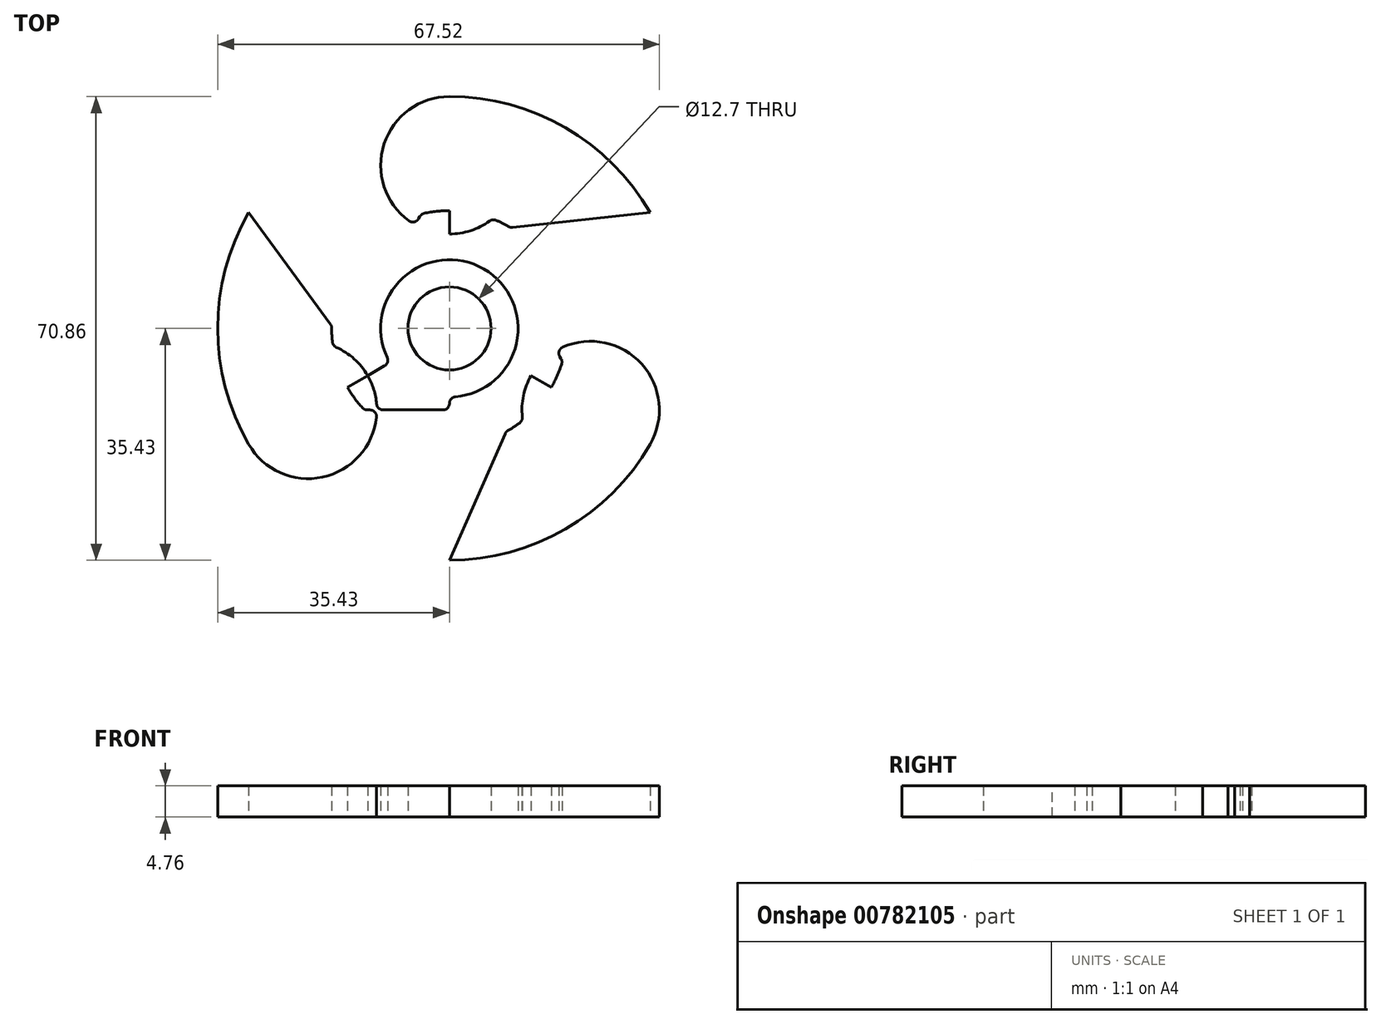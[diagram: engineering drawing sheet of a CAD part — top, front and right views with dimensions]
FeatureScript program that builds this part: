
annotation { "Feature Type Name" : "Feature", "Feature Type Description" : "" }
export const myFeature = defineFeature(function(context is Context, id is Id, definition is map)
    precondition{}
    {
        {
            var Q0;
            Q0=qCreatedBy(makeId("Top.planeOp"),FACE);
            var sketch = newSketch(context, id + "F0", { "sketchPlane" : qUnion([Q0])});
            skCircle(sketch, "E0", {"center": v(0, 0) * mm, "radius": 6.35 * mm});
            skCircle(sketch, "E1", {"center": v(0, 0) * mm, "radius": 10.5 * mm});
            skCircle(sketch, "E2", {"center": v(0, 0) * mm, "radius": 18 * mm});
            skCircle(sketch, "E3", {"center": v(0, 0) * mm, "radius": 24.93 * mm});
            skLineSegment(sketch, "E4", {"start": v(0, 0) * mm, "end": v(21.6, -12.46) * mm});
            skLineSegment(sketch, "E5", {"start": v(0, 0) * mm, "end": v(-21.59, -12.46) * mm});
            skLineSegment(sketch, "E6", {"start": v(0, 0) * mm, "end": v(0, 24.93) * mm});
            skLineSegment(sketch, "E7", {"start": v(0, 24.93) * mm, "end": v(-21.6, -12.46) * mm});
            skLineSegment(sketch, "E8", {"start": v(-21.59, -12.46) * mm, "end": v(21.59, -12.46) * mm});
            skLineSegment(sketch, "E9", {"start": v(0, 24.93) * mm, "end": v(21.6, -12.46) * mm});
            skCircle(sketch, "E10", {"center": v(0, 24.93) * mm, "radius": 10.5 * mm});
            skCircle(sketch, "E11", {"center": v(21.6, -12.46) * mm, "radius": 10.5 * mm});
            skCircle(sketch, "E12", {"center": v(-21.59, -12.46) * mm, "radius": 10.5 * mm});
            skCircle(sketch, "E13", {"center": v(0, 0) * mm, "radius": 35.43 * mm});
            skLineSegment(sketch, "E14", {"start": v(0, 0) * mm, "end": v(-21.6, 12.46) * mm});
            skLineSegment(sketch, "E15", {"start": v(0, 0) * mm, "end": v(21.59, 12.46) * mm});
            skLineSegment(sketch, "E16", {"start": v(0, 0) * mm, "end": v(0, -24.93) * mm});
            skPoint(sketch, "E16.endSnap0", {"position": v(0, -12.46) * mm});
            skLineSegment(sketch, "E17", {"start": v(0, 0) * mm, "end": v(-30.68, -17.71) * mm});
            skLineSegment(sketch, "E18", {"start": v(0, 0) * mm, "end": v(30.68, -17.71) * mm});
            skLineSegment(sketch, "E19", {"start": v(0, 0) * mm, "end": v(0, 35.43) * mm});
            skLineSegment(sketch, "E20", {"start": v(0, 0) * mm, "end": v(-30.68, 17.71) * mm});
            skLineSegment(sketch, "E21", {"start": v(0, 0) * mm, "end": v(0, -35.43) * mm});
            skLineSegment(sketch, "E22", {"start": v(0, 0) * mm, "end": v(30.68, 17.71) * mm});
            skLineSegment(sketch, "E23", {"start": v(-30.68, 17.71) * mm, "end": v(-13.14, -6.23) * mm});
            skPoint(sketch, "E23.endSnap0", {"position": v(-10.8, -6.23) * mm});
            skLineSegment(sketch, "E24", {"start": v(30.68, 17.71) * mm, "end": v(0, 14.37) * mm});
            skLineSegment(sketch, "E25", {"start": v(0, -35.43) * mm, "end": v(12.44, -7.18) * mm});
            skSolve(sketch);
        }
        {
            var Q0;
            {var subQ0=sQuery(id+"F0.wireOp",EDGE,"E20");var subQ1=sQuery(id+"F0.wireOp",EDGE,"E0");var subQ2=makeQuery(id+"F0.imprint","INTERSECT",VERTEX,{"derivedFrom":[subQ1,subQ0]});Q0=makeQuery(id+"F0.imprint","IMPRINT",FACE,{"disambiguationData":[TD([[makeQuery(id+"F0.imprint","IMPRINT",EDGE,{"disambiguationData":[TD([[subQ2,-1.0]])],"derivedFrom":subQ1}),-1.0]])]});}
            var Q1;
            {var subQ0=sQuery(id+"F0.wireOp",EDGE,"E17");var subQ1=sQuery(id+"F0.wireOp",EDGE,"E0");var subQ2=makeQuery(id+"F0.imprint","INTERSECT",VERTEX,{"derivedFrom":[subQ1,subQ0]});Q1=makeQuery(id+"F0.imprint","IMPRINT",FACE,{"disambiguationData":[TD([[makeQuery(id+"F0.imprint","IMPRINT",EDGE,{"disambiguationData":[TD([[subQ2,-1.0]])],"derivedFrom":subQ1}),-1.0]])]});}
            var Q2;
            {var subQ0=sQuery(id+"F0.wireOp",EDGE,"E21");var subQ1=sQuery(id+"F0.wireOp",EDGE,"E0");var subQ2=makeQuery(id+"F0.imprint","INTERSECT",VERTEX,{"derivedFrom":[subQ1,subQ0]});Q2=makeQuery(id+"F0.imprint","IMPRINT",FACE,{"disambiguationData":[TD([[makeQuery(id+"F0.imprint","IMPRINT",EDGE,{"disambiguationData":[TD([[subQ2,-1.0]])],"derivedFrom":subQ1}),-1.0]])]});}
            var Q3;
            {var subQ0=sQuery(id+"F0.wireOp",EDGE,"E22");var subQ1=sQuery(id+"F0.wireOp",EDGE,"E0");var subQ2=makeQuery(id+"F0.imprint","INTERSECT",VERTEX,{"derivedFrom":[subQ1,subQ0]});Q3=makeQuery(id+"F0.imprint","IMPRINT",FACE,{"disambiguationData":[TD([[makeQuery(id+"F0.imprint","IMPRINT",EDGE,{"disambiguationData":[TD([[subQ2,1.0]])],"derivedFrom":subQ1}),-1.0]])]});}
            var Q4;
            {var subQ0=sQuery(id+"F0.wireOp",EDGE,"E19");var subQ1=sQuery(id+"F0.wireOp",EDGE,"E0");var subQ2=makeQuery(id+"F0.imprint","INTERSECT",VERTEX,{"derivedFrom":[subQ1,subQ0]});Q4=makeQuery(id+"F0.imprint","IMPRINT",FACE,{"disambiguationData":[TD([[makeQuery(id+"F0.imprint","IMPRINT",EDGE,{"disambiguationData":[TD([[subQ2,1.0]])],"derivedFrom":subQ1}),-1.0]])]});}
            var Q5;
            {var subQ0=sQuery(id+"F0.wireOp",EDGE,"E19");var subQ1=sQuery(id+"F0.wireOp",EDGE,"E0");var subQ2=makeQuery(id+"F0.imprint","INTERSECT",VERTEX,{"derivedFrom":[subQ1,subQ0]});Q5=makeQuery(id+"F0.imprint","IMPRINT",FACE,{"disambiguationData":[TD([[makeQuery(id+"F0.imprint","IMPRINT",EDGE,{"disambiguationData":[TD([[subQ2,-1.0]])],"derivedFrom":subQ1}),-1.0]])]});}
            var Q6;
            {var subQ1=sQuery(id+"F0.wireOp",EDGE,"E3");var subQ3=sQuery(id+"F0.wireOp",EDGE,"E12");var subQ4=makeQuery(id+"F0.imprint","INTERSECT",VERTEX,{"disambiguationData":[OD(0.0)],"derivedFrom":[subQ1,subQ3]});Q6=makeQuery(id+"F0.imprint","IMPRINT",FACE,{"disambiguationData":[TD([[makeQuery(id+"F0.imprint","IMPRINT",EDGE,{"disambiguationData":[TD([[subQ4,-1.0]])],"derivedFrom":subQ3}),1.0]])]});}
            var Q7;
            {var subQ1=sQuery(id+"F0.wireOp",EDGE,"E3");var subQ3=sQuery(id+"F0.wireOp",EDGE,"E12");var subQ4=makeQuery(id+"F0.imprint","INTERSECT",VERTEX,{"disambiguationData":[OD(1.0)],"derivedFrom":[subQ1,subQ3]});Q7=makeQuery(id+"F0.imprint","IMPRINT",FACE,{"disambiguationData":[TD([[makeQuery(id+"F0.imprint","IMPRINT",EDGE,{"disambiguationData":[TD([[subQ4,1.0]])],"derivedFrom":subQ3}),1.0]])]});}
            var Q8;
            {var subQ0=sQuery(id+"F0.wireOp",EDGE,"E23");var subQ1=sQuery(id+"F0.wireOp",EDGE,"E3");var subQ2=makeQuery(id+"F0.imprint","INTERSECT",VERTEX,{"derivedFrom":[subQ1,subQ0]});Q8=makeQuery(id+"F0.imprint","IMPRINT",FACE,{"disambiguationData":[TD([[makeQuery(id+"F0.imprint","IMPRINT",EDGE,{"disambiguationData":[TD([[subQ2,-1.0]])],"derivedFrom":subQ1}),-1.0]])]});}
            var Q9;
            {var subQ0=sQuery(id+"F0.wireOp",EDGE,"E23");var subQ1=sQuery(id+"F0.wireOp",EDGE,"E2");var subQ2=makeQuery(id+"F0.imprint","INTERSECT",VERTEX,{"derivedFrom":[subQ1,subQ0]});Q9=makeQuery(id+"F0.imprint","IMPRINT",FACE,{"disambiguationData":[TD([[makeQuery(id+"F0.imprint","IMPRINT",EDGE,{"disambiguationData":[TD([[subQ2,-1.0]])],"derivedFrom":subQ1}),-1.0]])]});}
            var Q10;
            {var subQ0=sQuery(id+"F0.wireOp",EDGE,"E12");var subQ1=sQuery(id+"F0.wireOp",EDGE,"E2");var subQ2=makeQuery(id+"F0.imprint","INTERSECT",VERTEX,{"disambiguationData":[OD(0.0)],"derivedFrom":[subQ1,subQ0]});Q10=makeQuery(id+"F0.imprint","IMPRINT",FACE,{"disambiguationData":[TD([[makeQuery(id+"F0.imprint","IMPRINT",EDGE,{"disambiguationData":[TD([[subQ2,-1.0]])],"derivedFrom":subQ1}),-1.0]])]});}
            var Q11;
            {var subQ0=sQuery(id+"F0.wireOp",EDGE,"E8");var subQ1=sQuery(id+"F0.wireOp",EDGE,"E2");var subQ2=makeQuery(id+"F0.imprint","INTERSECT",VERTEX,{"disambiguationData":[OD(0.0)],"derivedFrom":[subQ1,subQ0]});Q11=makeQuery(id+"F0.imprint","IMPRINT",FACE,{"disambiguationData":[TD([[makeQuery(id+"F0.imprint","IMPRINT",EDGE,{"disambiguationData":[TD([[subQ2,-1.0]])],"derivedFrom":subQ1}),-1.0]])]});}
            var Q12;
            {var subQ0=sQuery(id+"F0.wireOp",EDGE,"E17");var subQ1=sQuery(id+"F0.wireOp",EDGE,"E2");var subQ2=makeQuery(id+"F0.imprint","INTERSECT",VERTEX,{"derivedFrom":[subQ1,subQ0]});Q12=makeQuery(id+"F0.imprint","IMPRINT",FACE,{"disambiguationData":[TD([[makeQuery(id+"F0.imprint","IMPRINT",EDGE,{"disambiguationData":[TD([[subQ2,-1.0]])],"derivedFrom":subQ1}),-1.0]])]});}
            var Q13;
            {var subQ0=sQuery(id+"F0.wireOp",EDGE,"E7");var subQ1=sQuery(id+"F0.wireOp",EDGE,"E2");var subQ2=makeQuery(id+"F0.imprint","INTERSECT",VERTEX,{"disambiguationData":[OD(1.0)],"derivedFrom":[subQ1,subQ0]});Q13=makeQuery(id+"F0.imprint","IMPRINT",FACE,{"disambiguationData":[TD([[makeQuery(id+"F0.imprint","IMPRINT",EDGE,{"disambiguationData":[TD([[subQ2,-1.0]])],"derivedFrom":subQ1}),-1.0]])]});}
            var Q14;
            {var subQ2=sQuery(id+"F0.wireOp",EDGE,"E7");var subQ6=sQuery(id+"F0.wireOp",EDGE,"E2");var subQ7=makeQuery(id+"F0.imprint","INTERSECT",VERTEX,{"disambiguationData":[OD(1.0)],"derivedFrom":[subQ6,subQ2]});Q14=makeQuery(id+"F0.imprint","IMPRINT",FACE,{"disambiguationData":[TD([[makeQuery(id+"F0.imprint","IMPRINT",EDGE,{"disambiguationData":[TD([[subQ7,-1.0]])],"derivedFrom":subQ6}),1.0]])]});}
            var Q15;
            {var subQ0=sQuery(id+"F0.wireOp",EDGE,"E17");var subQ1=sQuery(id+"F0.wireOp",EDGE,"E2");var subQ2=makeQuery(id+"F0.imprint","INTERSECT",VERTEX,{"derivedFrom":[subQ1,subQ0]});Q15=makeQuery(id+"F0.imprint","IMPRINT",FACE,{"disambiguationData":[TD([[makeQuery(id+"F0.imprint","IMPRINT",EDGE,{"disambiguationData":[TD([[subQ2,-1.0]])],"derivedFrom":subQ1}),1.0]])]});}
            var Q16;
            {var subQ0=sQuery(id+"F0.wireOp",EDGE,"E12");var subQ1=sQuery(id+"F0.wireOp",EDGE,"E2");var subQ2=makeQuery(id+"F0.imprint","INTERSECT",VERTEX,{"disambiguationData":[OD(0.0)],"derivedFrom":[subQ1,subQ0]});Q16=makeQuery(id+"F0.imprint","IMPRINT",FACE,{"disambiguationData":[TD([[makeQuery(id+"F0.imprint","IMPRINT",EDGE,{"disambiguationData":[TD([[subQ2,-1.0]])],"derivedFrom":subQ1}),1.0]])]});}
            var Q17;
            {var subQ0=sQuery(id+"F0.wireOp",EDGE,"E8");var subQ1=sQuery(id+"F0.wireOp",EDGE,"E2");var subQ2=makeQuery(id+"F0.imprint","INTERSECT",VERTEX,{"disambiguationData":[OD(0.0)],"derivedFrom":[subQ1,subQ0]});Q17=makeQuery(id+"F0.imprint","IMPRINT",FACE,{"disambiguationData":[TD([[makeQuery(id+"F0.imprint","IMPRINT",EDGE,{"disambiguationData":[TD([[subQ2,-1.0]])],"derivedFrom":subQ1}),1.0]])]});}
            var Q18;
            {var subQ0=sQuery(id+"F0.wireOp",EDGE,"E18");var subQ1=sQuery(id+"F0.wireOp",EDGE,"E2");var subQ2=makeQuery(id+"F0.imprint","INTERSECT",VERTEX,{"derivedFrom":[subQ1,subQ0]});Q18=makeQuery(id+"F0.imprint","IMPRINT",FACE,{"disambiguationData":[TD([[makeQuery(id+"F0.imprint","IMPRINT",EDGE,{"disambiguationData":[TD([[subQ2,-1.0]])],"derivedFrom":subQ1}),-1.0]])]});}
            var Q19;
            {var subQ0=sQuery(id+"F0.wireOp",EDGE,"E18");var subQ1=sQuery(id+"F0.wireOp",EDGE,"E2");var subQ2=makeQuery(id+"F0.imprint","INTERSECT",VERTEX,{"derivedFrom":[subQ1,subQ0]});Q19=makeQuery(id+"F0.imprint","IMPRINT",FACE,{"disambiguationData":[TD([[makeQuery(id+"F0.imprint","IMPRINT",EDGE,{"disambiguationData":[TD([[subQ2,-1.0]])],"derivedFrom":subQ1}),1.0]])]});}
            var Q20;
            {var subQ1=sQuery(id+"F0.wireOp",EDGE,"E8");var subQ4=sQuery(id+"F0.wireOp",EDGE,"E2");var subQ5=makeQuery(id+"F0.imprint","INTERSECT",VERTEX,{"disambiguationData":[OD(1.0)],"derivedFrom":[subQ4,subQ1]});Q20=makeQuery(id+"F0.imprint","IMPRINT",FACE,{"disambiguationData":[TD([[makeQuery(id+"F0.imprint","IMPRINT",EDGE,{"disambiguationData":[TD([[subQ5,-1.0]])],"derivedFrom":subQ4}),1.0]])]});}
            var Q21;
            {var subQ0=sQuery(id+"F0.wireOp",EDGE,"E8");var subQ1=sQuery(id+"F0.wireOp",EDGE,"E2");var subQ2=makeQuery(id+"F0.imprint","INTERSECT",VERTEX,{"disambiguationData":[OD(1.0)],"derivedFrom":[subQ1,subQ0]});Q21=makeQuery(id+"F0.imprint","IMPRINT",FACE,{"disambiguationData":[TD([[makeQuery(id+"F0.imprint","IMPRINT",EDGE,{"disambiguationData":[TD([[subQ2,-1.0]])],"derivedFrom":subQ1}),-1.0]])]});}
            var Q22;
            {var subQ0=sQuery(id+"F0.wireOp",EDGE,"E11");var subQ1=sQuery(id+"F0.wireOp",EDGE,"E2");var subQ2=makeQuery(id+"F0.imprint","INTERSECT",VERTEX,{"disambiguationData":[OD(0.0)],"derivedFrom":[subQ1,subQ0]});Q22=makeQuery(id+"F0.imprint","IMPRINT",FACE,{"disambiguationData":[TD([[makeQuery(id+"F0.imprint","IMPRINT",EDGE,{"disambiguationData":[TD([[subQ2,-1.0]])],"derivedFrom":subQ1}),-1.0]])]});}
            var Q23;
            {var subQ1=sQuery(id+"F0.wireOp",EDGE,"E3");var subQ3=sQuery(id+"F0.wireOp",EDGE,"E11");var subQ4=makeQuery(id+"F0.imprint","INTERSECT",VERTEX,{"disambiguationData":[OD(1.0)],"derivedFrom":[subQ1,subQ3]});Q23=makeQuery(id+"F0.imprint","IMPRINT",FACE,{"disambiguationData":[TD([[makeQuery(id+"F0.imprint","IMPRINT",EDGE,{"disambiguationData":[TD([[subQ4,1.0]])],"derivedFrom":subQ3}),1.0]])]});}
            var Q24;
            {var subQ0=sQuery(id+"F0.wireOp",EDGE,"E9");var subQ1=sQuery(id+"F0.wireOp",EDGE,"E2");var subQ2=makeQuery(id+"F0.imprint","INTERSECT",VERTEX,{"disambiguationData":[OD(1.0)],"derivedFrom":[subQ1,subQ0]});Q24=makeQuery(id+"F0.imprint","IMPRINT",FACE,{"disambiguationData":[TD([[makeQuery(id+"F0.imprint","IMPRINT",EDGE,{"disambiguationData":[TD([[subQ2,-1.0]])],"derivedFrom":subQ1}),-1.0]])]});}
            var Q25;
            {var subQ0=sQuery(id+"F0.wireOp",EDGE,"E9");var subQ1=sQuery(id+"F0.wireOp",EDGE,"E2");var subQ2=makeQuery(id+"F0.imprint","INTERSECT",VERTEX,{"disambiguationData":[OD(1.0)],"derivedFrom":[subQ1,subQ0]});Q25=makeQuery(id+"F0.imprint","IMPRINT",FACE,{"disambiguationData":[TD([[makeQuery(id+"F0.imprint","IMPRINT",EDGE,{"disambiguationData":[TD([[subQ2,-1.0]])],"derivedFrom":subQ1}),1.0]])]});}
            var Q26;
            {var subQ0=sQuery(id+"F0.wireOp",EDGE,"E25");var subQ1=sQuery(id+"F0.wireOp",EDGE,"E3");var subQ2=makeQuery(id+"F0.imprint","INTERSECT",VERTEX,{"derivedFrom":[subQ1,subQ0]});Q26=makeQuery(id+"F0.imprint","IMPRINT",FACE,{"disambiguationData":[TD([[makeQuery(id+"F0.imprint","IMPRINT",EDGE,{"disambiguationData":[TD([[subQ2,-1.0]])],"derivedFrom":subQ1}),-1.0]])]});}
            var Q27;
            {var subQ0=sQuery(id+"F0.wireOp",EDGE,"E25");var subQ1=sQuery(id+"F0.wireOp",EDGE,"E2");var subQ2=makeQuery(id+"F0.imprint","INTERSECT",VERTEX,{"derivedFrom":[subQ1,subQ0]});Q27=makeQuery(id+"F0.imprint","IMPRINT",FACE,{"disambiguationData":[TD([[makeQuery(id+"F0.imprint","IMPRINT",EDGE,{"disambiguationData":[TD([[subQ2,-1.0]])],"derivedFrom":subQ1}),-1.0]])]});}
            var Q28;
            {var subQ0=sQuery(id+"F0.wireOp",EDGE,"E11");var subQ1=sQuery(id+"F0.wireOp",EDGE,"E2");var subQ2=makeQuery(id+"F0.imprint","INTERSECT",VERTEX,{"disambiguationData":[OD(0.0)],"derivedFrom":[subQ1,subQ0]});Q28=makeQuery(id+"F0.imprint","IMPRINT",FACE,{"disambiguationData":[TD([[makeQuery(id+"F0.imprint","IMPRINT",EDGE,{"disambiguationData":[TD([[subQ2,-1.0]])],"derivedFrom":subQ1}),1.0]])]});}
            var Q29;
            {var subQ1=sQuery(id+"F0.wireOp",EDGE,"E3");var subQ3=sQuery(id+"F0.wireOp",EDGE,"E11");var subQ4=makeQuery(id+"F0.imprint","INTERSECT",VERTEX,{"disambiguationData":[OD(0.0)],"derivedFrom":[subQ1,subQ3]});Q29=makeQuery(id+"F0.imprint","IMPRINT",FACE,{"disambiguationData":[TD([[makeQuery(id+"F0.imprint","IMPRINT",EDGE,{"disambiguationData":[TD([[subQ4,-1.0]])],"derivedFrom":subQ3}),1.0]])]});}
            var Q30;
            {var subQ1=sQuery(id+"F0.wireOp",EDGE,"E9");var subQ4=sQuery(id+"F0.wireOp",EDGE,"E2");var subQ5=makeQuery(id+"F0.imprint","INTERSECT",VERTEX,{"disambiguationData":[OD(0.0)],"derivedFrom":[subQ4,subQ1]});Q30=makeQuery(id+"F0.imprint","IMPRINT",FACE,{"disambiguationData":[TD([[makeQuery(id+"F0.imprint","IMPRINT",EDGE,{"disambiguationData":[TD([[subQ5,-1.0]])],"derivedFrom":subQ4}),1.0]])]});}
            var Q31;
            {var subQ0=sQuery(id+"F0.wireOp",EDGE,"E19");var subQ1=sQuery(id+"F0.wireOp",EDGE,"E2");var subQ2=makeQuery(id+"F0.imprint","INTERSECT",VERTEX,{"derivedFrom":[subQ1,subQ0]});Q31=makeQuery(id+"F0.imprint","IMPRINT",FACE,{"disambiguationData":[TD([[makeQuery(id+"F0.imprint","IMPRINT",EDGE,{"disambiguationData":[TD([[subQ2,-1.0]])],"derivedFrom":subQ1}),-1.0]])]});}
            var Q32;
            {var subQ0=sQuery(id+"F0.wireOp",EDGE,"E9");var subQ1=sQuery(id+"F0.wireOp",EDGE,"E2");var subQ2=makeQuery(id+"F0.imprint","INTERSECT",VERTEX,{"disambiguationData":[OD(0.0)],"derivedFrom":[subQ1,subQ0]});Q32=makeQuery(id+"F0.imprint","IMPRINT",FACE,{"disambiguationData":[TD([[makeQuery(id+"F0.imprint","IMPRINT",EDGE,{"disambiguationData":[TD([[subQ2,-1.0]])],"derivedFrom":subQ1}),-1.0]])]});}
            var Q33;
            {var subQ0=sQuery(id+"F0.wireOp",EDGE,"E7");var subQ1=sQuery(id+"F0.wireOp",EDGE,"E2");var subQ2=makeQuery(id+"F0.imprint","INTERSECT",VERTEX,{"disambiguationData":[OD(0.0)],"derivedFrom":[subQ1,subQ0]});Q33=makeQuery(id+"F0.imprint","IMPRINT",FACE,{"disambiguationData":[TD([[makeQuery(id+"F0.imprint","IMPRINT",EDGE,{"disambiguationData":[TD([[subQ2,-1.0]])],"derivedFrom":subQ1}),1.0]])]});}
            var Q34;
            {var subQ0=sQuery(id+"F0.wireOp",EDGE,"E10");var subQ1=sQuery(id+"F0.wireOp",EDGE,"E2");var subQ2=makeQuery(id+"F0.imprint","INTERSECT",VERTEX,{"disambiguationData":[OD(0.0)],"derivedFrom":[subQ1,subQ0]});Q34=makeQuery(id+"F0.imprint","IMPRINT",FACE,{"disambiguationData":[TD([[makeQuery(id+"F0.imprint","IMPRINT",EDGE,{"disambiguationData":[TD([[subQ2,-1.0]])],"derivedFrom":subQ1}),-1.0]])]});}
            var Q35;
            {var subQ0=sQuery(id+"F0.wireOp",EDGE,"E10");var subQ1=sQuery(id+"F0.wireOp",EDGE,"E2");var subQ2=makeQuery(id+"F0.imprint","INTERSECT",VERTEX,{"disambiguationData":[OD(0.0)],"derivedFrom":[subQ1,subQ0]});Q35=makeQuery(id+"F0.imprint","IMPRINT",FACE,{"disambiguationData":[TD([[makeQuery(id+"F0.imprint","IMPRINT",EDGE,{"disambiguationData":[TD([[subQ2,-1.0]])],"derivedFrom":subQ1}),1.0]])]});}
            var Q36;
            {var subQ0=sQuery(id+"F0.wireOp",EDGE,"E19");var subQ1=sQuery(id+"F0.wireOp",EDGE,"E2");var subQ2=makeQuery(id+"F0.imprint","INTERSECT",VERTEX,{"derivedFrom":[subQ1,subQ0]});Q36=makeQuery(id+"F0.imprint","IMPRINT",FACE,{"disambiguationData":[TD([[makeQuery(id+"F0.imprint","IMPRINT",EDGE,{"disambiguationData":[TD([[subQ2,-1.0]])],"derivedFrom":subQ1}),1.0]])]});}
            var Q37;
            {var subQ0=sQuery(id+"F0.wireOp",EDGE,"E7");var subQ1=sQuery(id+"F0.wireOp",EDGE,"E2");var subQ2=makeQuery(id+"F0.imprint","INTERSECT",VERTEX,{"disambiguationData":[OD(0.0)],"derivedFrom":[subQ1,subQ0]});Q37=makeQuery(id+"F0.imprint","IMPRINT",FACE,{"disambiguationData":[TD([[makeQuery(id+"F0.imprint","IMPRINT",EDGE,{"disambiguationData":[TD([[subQ2,-1.0]])],"derivedFrom":subQ1}),-1.0]])]});}
            var Q38;
            {var subQ1=sQuery(id+"F0.wireOp",EDGE,"E3");var subQ3=sQuery(id+"F0.wireOp",EDGE,"E10");var subQ4=makeQuery(id+"F0.imprint","INTERSECT",VERTEX,{"disambiguationData":[OD(1.0)],"derivedFrom":[subQ1,subQ3]});Q38=makeQuery(id+"F0.imprint","IMPRINT",FACE,{"disambiguationData":[TD([[makeQuery(id+"F0.imprint","IMPRINT",EDGE,{"disambiguationData":[TD([[subQ4,1.0]])],"derivedFrom":subQ3}),1.0]])]});}
            var Q39;
            {var subQ1=sQuery(id+"F0.wireOp",EDGE,"E3");var subQ3=sQuery(id+"F0.wireOp",EDGE,"E10");var subQ4=makeQuery(id+"F0.imprint","INTERSECT",VERTEX,{"disambiguationData":[OD(0.0)],"derivedFrom":[subQ1,subQ3]});Q39=makeQuery(id+"F0.imprint","IMPRINT",FACE,{"disambiguationData":[TD([[makeQuery(id+"F0.imprint","IMPRINT",EDGE,{"disambiguationData":[TD([[subQ4,-1.0]])],"derivedFrom":subQ3}),1.0]])]});}
            var Q40;
            {var subQ0=sQuery(id+"F0.wireOp",EDGE,"E24");var subQ1=sQuery(id+"F0.wireOp",EDGE,"E3");var subQ2=makeQuery(id+"F0.imprint","INTERSECT",VERTEX,{"derivedFrom":[subQ1,subQ0]});Q40=makeQuery(id+"F0.imprint","IMPRINT",FACE,{"disambiguationData":[TD([[makeQuery(id+"F0.imprint","IMPRINT",EDGE,{"disambiguationData":[TD([[subQ2,-1.0]])],"derivedFrom":subQ1}),-1.0]])]});}
            var Q41;
            {var subQ0=sQuery(id+"F0.wireOp",EDGE,"E24");var subQ1=sQuery(id+"F0.wireOp",EDGE,"E2");var subQ2=makeQuery(id+"F0.imprint","INTERSECT",VERTEX,{"derivedFrom":[subQ1,subQ0]});Q41=makeQuery(id+"F0.imprint","IMPRINT",FACE,{"disambiguationData":[TD([[makeQuery(id+"F0.imprint","IMPRINT",EDGE,{"disambiguationData":[TD([[subQ2,-1.0]])],"derivedFrom":subQ1}),-1.0]])]});}
            var Q42;
            {var subQ5=sQuery(id+"F0.wireOp",EDGE,"E19");var subQ8=sQuery(id+"F0.wireOp",EDGE,"E1");var subQ9=makeQuery(id+"F0.imprint","INTERSECT",VERTEX,{"derivedFrom":[subQ8,subQ5]});Q42=makeQuery(id+"F0.imprint","IMPRINT",FACE,{"disambiguationData":[TD([[makeQuery(id+"F0.imprint","IMPRINT",EDGE,{"disambiguationData":[TD([[subQ9,-1.0]])],"derivedFrom":subQ8}),-1.0]])]});}
            var Q43;
            {var subQ2=sQuery(id+"F0.wireOp",EDGE,"E1");var subQ4=sQuery(id+"F0.wireOp",EDGE,"E22");var subQ9=makeQuery(id+"F0.imprint","INTERSECT",VERTEX,{"derivedFrom":[subQ2,subQ4]});Q43=makeQuery(id+"F0.imprint","IMPRINT",FACE,{"disambiguationData":[TD([[makeQuery(id+"F0.imprint","IMPRINT",EDGE,{"disambiguationData":[TD([[subQ9,1.0]])],"derivedFrom":subQ2}),-1.0]])]});}
            var Q44;
            {var subQ3=sQuery(id+"F0.wireOp",EDGE,"E17");var subQ7=sQuery(id+"F0.wireOp",EDGE,"E1");var subQ8=makeQuery(id+"F0.imprint","INTERSECT",VERTEX,{"derivedFrom":[subQ7,subQ3]});Q44=makeQuery(id+"F0.imprint","IMPRINT",FACE,{"disambiguationData":[TD([[makeQuery(id+"F0.imprint","IMPRINT",EDGE,{"disambiguationData":[TD([[subQ8,-1.0]])],"derivedFrom":subQ7}),-1.0]])]});}
            extrude(context, id + "F1", {"entities" : qUnion([Q0, Q1, Q2, Q3, Q4, Q5, Q6, Q7, Q8, Q9, Q10, Q11, Q12, Q13, Q14, Q15, Q16, Q17, Q18, Q19, Q20, Q21, Q22, Q23, Q24, Q25, Q26, Q27, Q28, Q29, Q30, Q31, Q32, Q33, Q34, Q35, Q36, Q37, Q38, Q39, Q40, Q41, Q42, Q43, Q44]), "depth" : 4.76 * mm, "offsetDistance" : 25.4 * mm});
        }
        {
            var Q0;
            Q0=makeQuery(id+"F1.opExtrude","SWEPT_EDGE",EDGE,{"disambiguationData":[OSD([sQuery(id+"F0.wireOp",EDGE,"E8"),sQuery(id+"F0.wireOp",EDGE,"E21")])]});
            var Q1;
            Q1=makeQuery(id+"F1.opExtrude","SWEPT_EDGE",EDGE,{"disambiguationData":[OSD([sQuery(id+"F0.wireOp",EDGE,"E9"),sQuery(id+"F0.wireOp",EDGE,"E22")])]});
            var Q2;
            Q2=makeQuery(id+"F1.opExtrude","SWEPT_EDGE",EDGE,{"disambiguationData":[OSD([sQuery(id+"F0.wireOp",EDGE,"E7"),sQuery(id+"F0.wireOp",EDGE,"E20")])]});
            var Q3;
            Q3=makeQuery(id+"F1.opExtrude","SWEPT_EDGE",EDGE,{"disambiguationData":[OSD([sQuery(id+"F0.wireOp",EDGE,"E2"),sQuery(id+"F0.wireOp",EDGE,"E25")])]});
            var Q4;
            Q4=makeQuery(id+"F1.opExtrude","SWEPT_EDGE",EDGE,{"disambiguationData":[OSD([sQuery(id+"F0.wireOp",EDGE,"E2"),sQuery(id+"F0.wireOp",EDGE,"E11")])]});
            var Q5;
            Q5=makeQuery(id+"F1.opExtrude","SWEPT_EDGE",EDGE,{"disambiguationData":[OSD([sQuery(id+"F0.wireOp",EDGE,"E2"),sQuery(id+"F0.wireOp",EDGE,"E23")])]});
            var Q6;
            Q6=makeQuery(id+"F1.opExtrude","SWEPT_EDGE",EDGE,{"disambiguationData":[OSD([sQuery(id+"F0.wireOp",EDGE,"E2"),sQuery(id+"F0.wireOp",EDGE,"E12")])]});
            var Q7;
            Q7=makeQuery(id+"F1.opExtrude","SWEPT_EDGE",EDGE,{"disambiguationData":[OSD([sQuery(id+"F0.wireOp",EDGE,"E2"),sQuery(id+"F0.wireOp",EDGE,"E24")])]});
            var Q8;
            Q8=makeQuery(id+"F1.opExtrude","SWEPT_EDGE",EDGE,{"disambiguationData":[OSD([sQuery(id+"F0.wireOp",EDGE,"E2"),sQuery(id+"F0.wireOp",EDGE,"E10")])]});
            var Q9;
            Q9=makeQuery(id+"F1.opExtrude","SWEPT_EDGE",EDGE,{"disambiguationData":[OSD([sQuery(id+"F0.wireOp",EDGE,"E10"),sQuery(id+"F0.wireOp",EDGE,"E19")])]});
            var Q10;
            Q10=makeQuery(id+"F1.opExtrude","SWEPT_EDGE",EDGE,{"disambiguationData":[OSD([sQuery(id+"F0.wireOp",EDGE,"E1"),sQuery(id+"F0.wireOp",EDGE,"E18")])]});
            var Q11;
            Q11=makeQuery(id+"F1.opExtrude","SWEPT_EDGE",EDGE,{"disambiguationData":[OSD([sQuery(id+"F0.wireOp",EDGE,"E1"),sQuery(id+"F0.wireOp",EDGE,"E21")])]});
            var Q12;
            Q12=makeQuery(id+"F1.opExtrude","SWEPT_EDGE",EDGE,{"disambiguationData":[OSD([sQuery(id+"F0.wireOp",EDGE,"E1"),sQuery(id+"F0.wireOp",EDGE,"E19")])]});
            var Q13;
            Q13=makeQuery(id+"F1.opExtrude","SWEPT_EDGE",EDGE,{"disambiguationData":[OSD([sQuery(id+"F0.wireOp",EDGE,"E1"),sQuery(id+"F0.wireOp",EDGE,"E17")])]});
            var Q14;
            Q14=makeQuery(id+"F1.opExtrude","SWEPT_EDGE",EDGE,{"disambiguationData":[OSD([sQuery(id+"F0.wireOp",EDGE,"E11"),sQuery(id+"F0.wireOp",EDGE,"E18")])]});
            var Q15;
            Q15=makeQuery(id+"F1.opExtrude","SWEPT_EDGE",EDGE,{"disambiguationData":[OSD([sQuery(id+"F0.wireOp",EDGE,"E1"),sQuery(id+"F0.wireOp",EDGE,"E20")])]});
            var Q16;
            Q16=makeQuery(id+"F1.opExtrude","SWEPT_EDGE",EDGE,{"disambiguationData":[OSD([sQuery(id+"F0.wireOp",EDGE,"E7"),sQuery(id+"F0.wireOp",EDGE,"E10")])]});
            var Q17;
            Q17=makeQuery(id+"F1.opExtrude","SWEPT_EDGE",EDGE,{"disambiguationData":[OSD([sQuery(id+"F0.wireOp",EDGE,"E8"),sQuery(id+"F0.wireOp",EDGE,"E12")])]});
            var Q18;
            Q18=makeQuery(id+"F1.opExtrude","SWEPT_EDGE",EDGE,{"disambiguationData":[OSD([sQuery(id+"F0.wireOp",EDGE,"E1"),sQuery(id+"F0.wireOp",EDGE,"E22")])]});
            var Q19;
            Q19=makeQuery(id+"F1.opExtrude","SWEPT_EDGE",EDGE,{"disambiguationData":[OSD([sQuery(id+"F0.wireOp",EDGE,"E12"),sQuery(id+"F0.wireOp",EDGE,"E17")])]});
            var Q20;
            Q20=makeQuery(id+"F1.opExtrude","SWEPT_EDGE",EDGE,{"disambiguationData":[OSD([sQuery(id+"F0.wireOp",EDGE,"E9"),sQuery(id+"F0.wireOp",EDGE,"E11")])]});
            fillet(context, id + "F2", {"entities" : qUnion([Q0, Q1, Q2, Q3, Q4, Q5, Q6, Q7, Q8, Q9, Q10, Q11, Q12, Q13, Q14, Q15, Q16, Q17, Q18, Q19, Q20]), "radius" : 1 * mm, "tangentPropagation" : true, "allowEdgeOverflow" : false});
        }
    });
